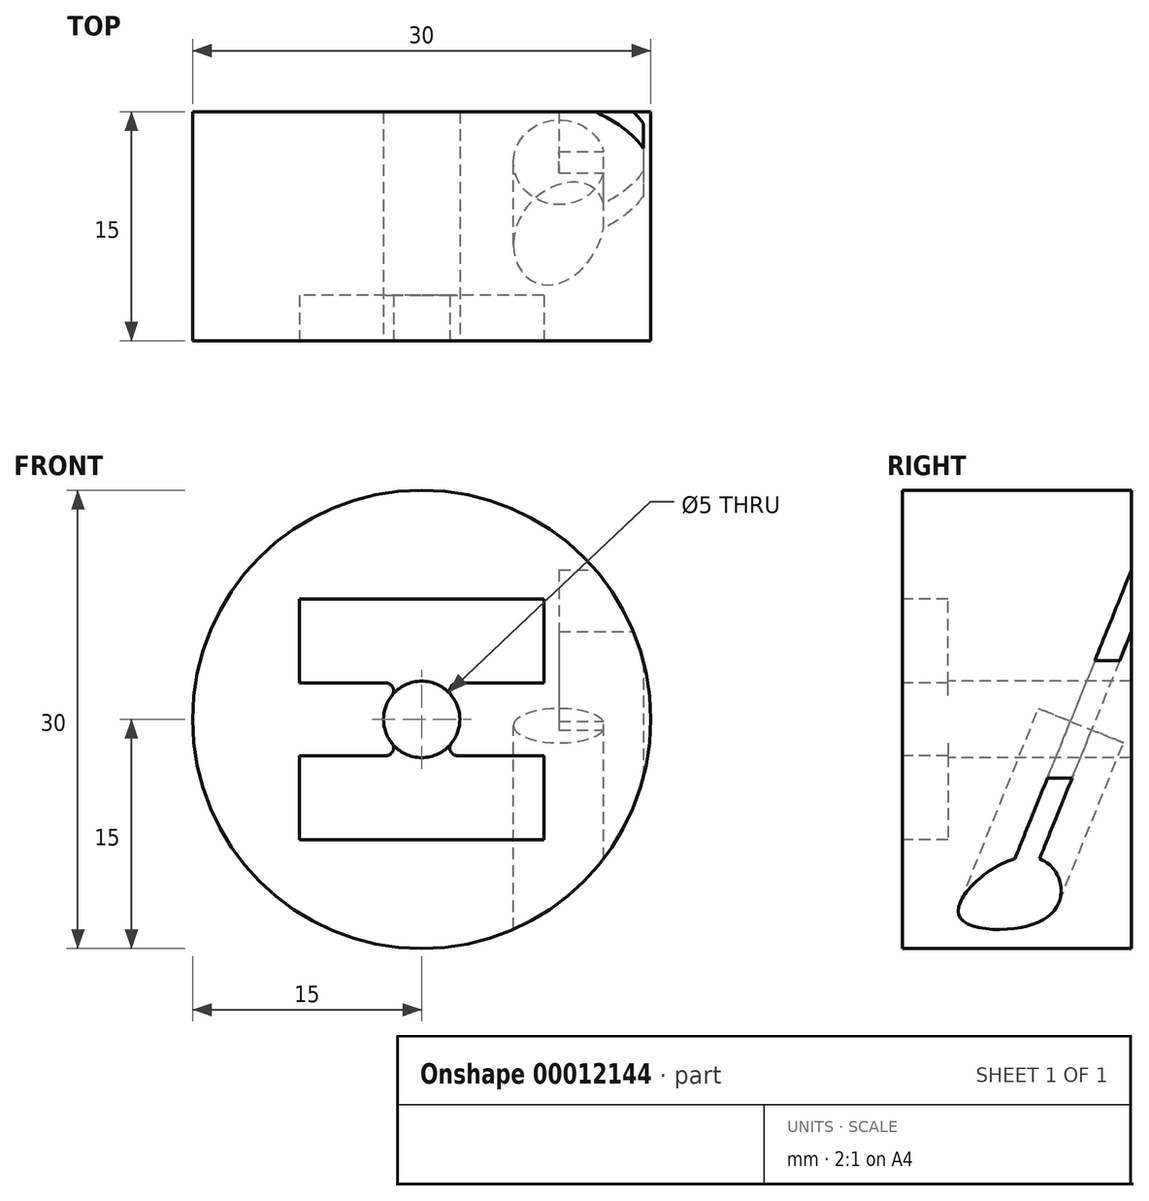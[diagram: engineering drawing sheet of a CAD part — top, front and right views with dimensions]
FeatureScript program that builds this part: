
annotation { "Feature Type Name" : "Feature", "Feature Type Description" : "" }
export const myFeature = defineFeature(function(context is Context, id is Id, definition is map)
    precondition{}
    {
        {
            var Q0;
            Q0=qCreatedBy(makeId("Front.planeOp"),FACE);
            var sketch = newSketch(context, id + "F0", { "sketchPlane" : qUnion([Q0])});
            skLineSegment(sketch, "E0.rect.bottom", {"start": v(8, -2.37) * mm, "end": v(2.34, -2.37) * mm});
            skLineSegment(sketch, "E0.rect.top", {"start": v(8, 2.38) * mm, "end": v(2.34, 2.38) * mm});
            skPoint(sketch, "E0.rect.middle", {"position": v(0, 0) * mm});
            skCircle(sketch, "E1", {"center": v(0, 0) * mm, "radius": 15 * mm});
            skLineSegment(sketch, "E2.top", {"start": v(8, -7.87) * mm, "end": v(-8, -7.88) * mm});
            skLineSegment(sketch, "E2.left", {"start": v(8, -2.37) * mm, "end": v(8, -7.87) * mm});
            skLineSegment(sketch, "E2.right", {"start": v(-8, -2.38) * mm, "end": v(-8, -7.88) * mm});
            skLineSegment(sketch, "E3.top", {"start": v(8, 7.88) * mm, "end": v(-8, 7.87) * mm});
            skLineSegment(sketch, "E3.left", {"start": v(8, 2.38) * mm, "end": v(8, 7.88) * mm});
            skLineSegment(sketch, "E3.right", {"start": v(-8, 2.37) * mm, "end": v(-8, 7.87) * mm});
            skArc(sketch, "E4", {"start": v(-1.95, 1.56) * mm, "mid": v(-2.5, 0) * mm, "end": v(-1.95, -1.56) * mm});
            skArc(sketch, "E5.trimOffspring", {"start": v(1.95, -1.56) * mm, "mid": v(2.5, 0) * mm, "end": v(1.95, 1.56) * mm});
            skLineSegment(sketch, "E6.trimOffspring", {"start": v(-2.34, -2.37) * mm, "end": v(-8, -2.38) * mm});
            skLineSegment(sketch, "E7.trimOffspring", {"start": v(-2.34, 2.38) * mm, "end": v(-8, 2.38) * mm});
            skLineSegment(sketch, "E8.trimOffspring", {"start": v(-2.34, -2.37) * mm, "end": v(-8, -2.37) * mm});
            skPoint(sketch, "E9.visualSharp", {"position": v(-0.78, 2.37) * mm});
            skArc(sketch, "E9.filletArc", {"start": v(-1.95, 1.56) * mm, "mid": v(-1.9, 2.1) * mm, "end": v(-2.34, 2.38) * mm});
            skPoint(sketch, "E10.visualSharp", {"position": v(-0.78, -2.37) * mm});
            skArc(sketch, "E10.filletArc", {"start": v(-2.34, -2.37) * mm, "mid": v(-1.9, -2.1) * mm, "end": v(-1.95, -1.56) * mm});
            skPoint(sketch, "E11.visualSharp", {"position": v(0.78, -2.37) * mm});
            skArc(sketch, "E11.filletArc", {"start": v(1.95, -1.56) * mm, "mid": v(1.9, -2.1) * mm, "end": v(2.34, -2.37) * mm});
            skPoint(sketch, "E12.visualSharp", {"position": v(0.78, 2.38) * mm});
            skArc(sketch, "E12.filletArc", {"start": v(2.34, 2.38) * mm, "mid": v(1.9, 2.1) * mm, "end": v(1.95, 1.56) * mm});
            skCircle(sketch, "E13", {"center": v(0, 0) * mm, "radius": 2.5 * mm});
            skLineSegment(sketch, "E14", {"start": v(0, 0) * mm, "end": v(22.49, 0) * mm});
            skSolve(sketch);
        }
        {
            var Q0;
            Q0=makeQuery(id+"F0.imprint","IMPRINT",FACE,{"disambiguationData":[TD([[makeQuery(id+"F0.imprint","IMPRINT",EDGE,{"derivedFrom":sQuery(id+"F0.wireOp",EDGE,"E0.rect.top")}),-1.0]])]});
            var Q1;
            {var subQ0=sQuery(id+"F0.wireOp",EDGE,"E13");var subQ4=makeQuery(id+"F0.imprint","INTERSECT",VERTEX,{"derivedFrom":[sQuery(id+"F0.wireOp",EDGE,"E9.filletArc"),subQ0]});Q1=makeQuery(id+"F0.imprint","IMPRINT",FACE,{"disambiguationData":[TD([[makeQuery(id+"F0.imprint","IMPRINT",EDGE,{"disambiguationData":[TD([[subQ4,1.0]])],"derivedFrom":subQ0}),1.0]])]});}
            var Q2;
            Q2=makeQuery(id+"F0.imprint","IMPRINT",FACE,{"disambiguationData":[TD([[makeQuery(id+"F0.imprint","IMPRINT",EDGE,{"derivedFrom":sQuery(id+"F0.wireOp",EDGE,"E1")}),1.0]])]});
            var Q3;
            Q3=makeQuery(id+"F0.imprint","IMPRINT",FACE,{"disambiguationData":[TD([[makeQuery(id+"F0.imprint","IMPRINT",EDGE,{"derivedFrom":sQuery(id+"F0.wireOp",EDGE,"E0.rect.bottom")}),1.0]])]});
            extrude(context, id + "F1", {"entities" : qUnion([Q0, Q1, Q2, Q3]), "oppositeDirection" : true, "depth" : 15 * mm});
        }
        {
            var Q0;
            Q0=makeQuery(id+"F0.imprint","IMPRINT",FACE,{"disambiguationData":[TD([[makeQuery(id+"F0.imprint","IMPRINT",EDGE,{"derivedFrom":sQuery(id+"F0.wireOp",EDGE,"E0.rect.top")}),-1.0]])]});
            var Q1;
            Q1=makeQuery(id+"F0.imprint","IMPRINT",FACE,{"disambiguationData":[TD([[makeQuery(id+"F0.imprint","IMPRINT",EDGE,{"derivedFrom":sQuery(id+"F0.wireOp",EDGE,"E0.rect.bottom")}),1.0]])]});
            extrude(context, id + "F2", {"entities" : qUnion([Q0, Q1]), "operationType" : NewBodyOperationType.REMOVE, "oppositeDirection" : true, "depth" : 3 * mm});
        }
        {
            var Q0;
            {var subQ0=sQuery(id+"F0.wireOp",EDGE,"E13");var subQ4=makeQuery(id+"F0.imprint","INTERSECT",VERTEX,{"derivedFrom":[sQuery(id+"F0.wireOp",EDGE,"E9.filletArc"),subQ0]});Q0=makeQuery(id+"F0.imprint","IMPRINT",FACE,{"disambiguationData":[TD([[makeQuery(id+"F0.imprint","IMPRINT",EDGE,{"disambiguationData":[TD([[subQ4,1.0]])],"derivedFrom":subQ0}),1.0]])]});}
            extrude(context, id + "F3", {"entities" : qUnion([Q0]), "operationType" : NewBodyOperationType.REMOVE, "endBound" : BoundingType.THROUGH_ALL, "oppositeDirection" : true, "depth" : 25 * mm});
        }
        {
            var Q0;
            Q0=qCreatedBy(makeId("Right.planeOp"),FACE);
            var sketch = newSketch(context, id + "F4", { "sketchPlane" : qUnion([Q0])});
            skLineSegment(sketch, "E15", {"start": v(0, 0) * mm, "end": v(50.88, -20.56) * mm});
            skSolve(sketch);
        }
        {
            var Q0;
            Q0=sQuery(id+"F0.wireOp",VERTEX,"E1.center");
            var Q1;
            Q1=sQuery(id+"F0.wireOp",VERTEX,"E14.end");
            var Q2;
            Q2=sQuery(id+"F4.wireOp",VERTEX,"E15.end");
            cPlane(context, id + "F5", {"entities" : qUnion([Q0, Q1, Q2]), "cplaneType" : CPlaneType.THREE_POINT, "offset" : 150 * mm, "width" : 150 * mm, "height" : 150 * mm});
        }
        {
            var Q0;
            Q0=qCreatedBy(id+"F5.planeOp",FACE);
            var sketch = newSketch(context, id + "F6", { "sketchPlane" : qUnion([Q0])});
            skCircle(sketch, "E16", {"center": v(9, -11) * mm, "radius": 3 * mm});
            skLineSegment(sketch, "E17.bottom", {"start": v(9, -10.25) * mm, "end": v(14.5, -10.25) * mm});
            skLineSegment(sketch, "E17.top", {"start": v(9, -11.75) * mm, "end": v(14.5, -11.75) * mm});
            skLineSegment(sketch, "E17.left", {"start": v(9, -10.25) * mm, "end": v(9, -11.75) * mm});
            skLineSegment(sketch, "E17.right", {"start": v(14.5, -10.25) * mm, "end": v(14.5, -11.75) * mm});
            skSolve(sketch);
        }
        {
            var Q0;
            {var subQ0=sQuery(id+"F6.wireOp",EDGE,"E17.left");Q0=makeQuery(id+"F6.imprint","IMPRINT",FACE,{"disambiguationData":[TD([[makeQuery(id+"F6.imprint","IMPRINT",EDGE,{"derivedFrom":subQ0}),-1.0]])]});}
            var Q1;
            {var subQ0=sQuery(id+"F6.wireOp",EDGE,"E17.left");Q1=makeQuery(id+"F6.imprint","IMPRINT",FACE,{"disambiguationData":[TD([[makeQuery(id+"F6.imprint","IMPRINT",EDGE,{"derivedFrom":subQ0}),1.0]])]});}
            extrude(context, id + "F7", {"entities" : qUnion([Q0, Q1]), "operationType" : NewBodyOperationType.REMOVE, "depth" : 25 * mm, "hasSecondDirection" : true, "secondDirectionOppositeDirection" : true, "secondDirectionDepth" : 4 * mm});
        }
        {
            var Q0;
            {var subQ0=sQuery(id+"F6.wireOp",EDGE,"E17.right");Q0=makeQuery(id+"F6.imprint","IMPRINT",FACE,{"disambiguationData":[TD([[makeQuery(id+"F6.imprint","IMPRINT",EDGE,{"derivedFrom":subQ0}),-1.0]])]});}
            var Q1;
            {var subQ0=sQuery(id+"F6.wireOp",EDGE,"E17.left");Q1=makeQuery(id+"F6.imprint","IMPRINT",FACE,{"disambiguationData":[TD([[makeQuery(id+"F6.imprint","IMPRINT",EDGE,{"derivedFrom":subQ0}),1.0]])]});}
            extrude(context, id + "F8", {"entities" : qUnion([Q0, Q1]), "operationType" : NewBodyOperationType.REMOVE, "endBound" : BoundingType.THROUGH_ALL, "oppositeDirection" : true, "depth" : 25 * mm, "hasSecondDirection" : true, "secondDirectionBound" : SecondDirectionBoundingType.THROUGH_ALL, "secondDirectionOppositeDirection" : false, "secondDirectionDepth" : 25 * mm});
        }
    });
